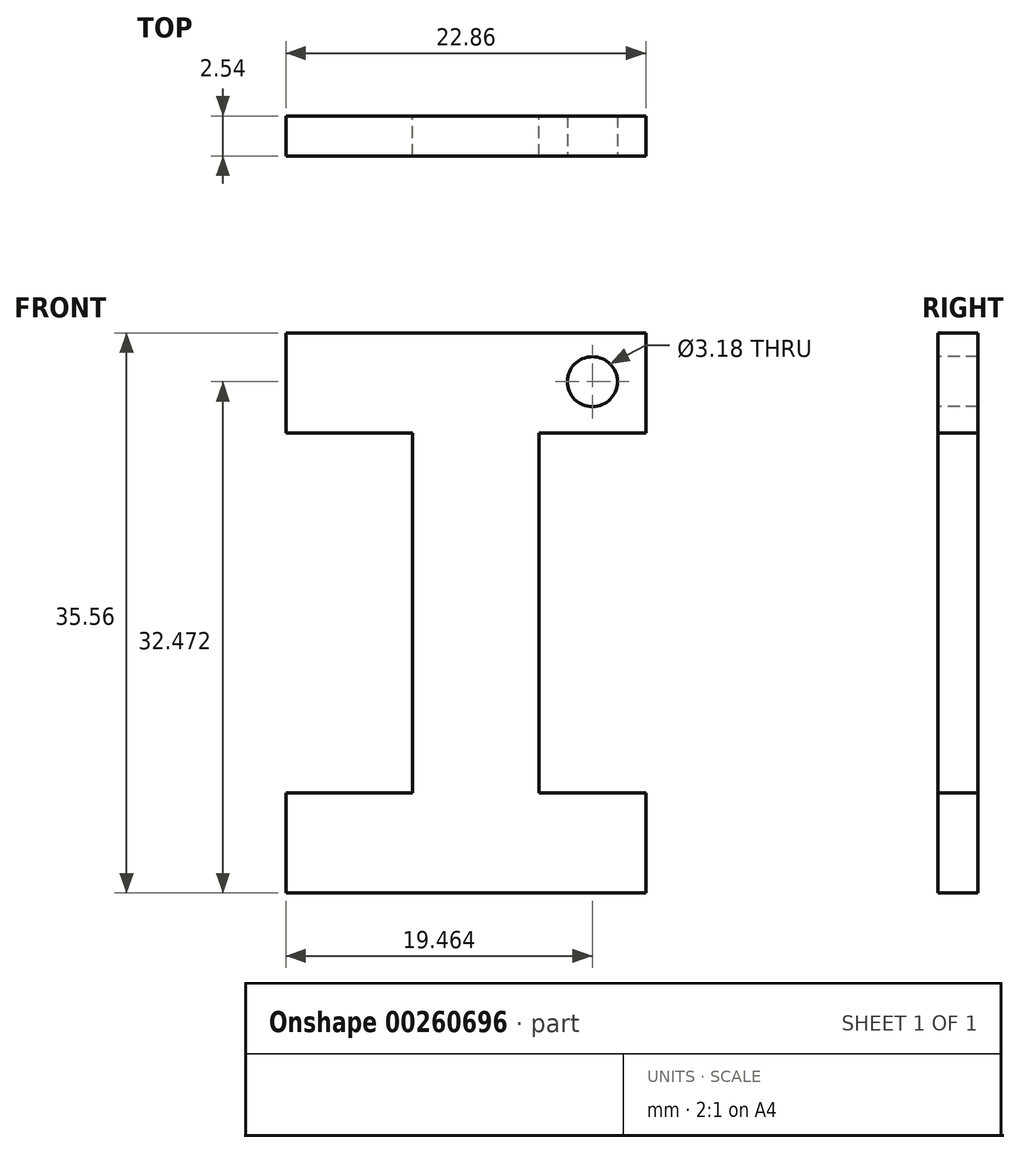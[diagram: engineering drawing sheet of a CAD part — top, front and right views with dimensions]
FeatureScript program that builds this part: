
annotation { "Feature Type Name" : "Feature", "Feature Type Description" : "" }
export const myFeature = defineFeature(function(context is Context, id is Id, definition is map)
    precondition{}
    {
        {
            var Q0;
            Q0=qCreatedBy(makeId("Front.planeOp"),FACE);
            var sketch = newSketch(context, id + "F0", { "sketchPlane" : qUnion([Q0])});
            skLineSegment(sketch, "E0", {"start": v(-12.96, 0) * mm, "end": v(-12.96, 6.35) * mm});
            skLineSegment(sketch, "E1", {"start": v(-12.96, 6.35) * mm, "end": v(-4.93, 6.35) * mm});
            skLineSegment(sketch, "E2", {"start": v(-4.93, 6.35) * mm, "end": v(-4.93, 29.21) * mm});
            skLineSegment(sketch, "E3", {"start": v(-4.93, 29.21) * mm, "end": v(-12.96, 29.21) * mm});
            skLineSegment(sketch, "E4", {"start": v(-12.96, 29.21) * mm, "end": v(-12.96, 35.56) * mm});
            skLineSegment(sketch, "E5", {"start": v(-12.96, 35.56) * mm, "end": v(9.9, 35.56) * mm});
            skLineSegment(sketch, "E6", {"start": v(9.9, 35.56) * mm, "end": v(9.9, 29.21) * mm});
            skLineSegment(sketch, "E7", {"start": v(9.9, 29.21) * mm, "end": v(3.11, 29.21) * mm});
            skLineSegment(sketch, "E8", {"start": v(3.11, 29.21) * mm, "end": v(3.11, 6.35) * mm});
            skLineSegment(sketch, "E9", {"start": v(3.11, 6.35) * mm, "end": v(9.9, 6.35) * mm});
            skLineSegment(sketch, "E10", {"start": v(9.9, 6.35) * mm, "end": v(9.9, 0) * mm});
            skLineSegment(sketch, "E11", {"start": v(9.9, 0) * mm, "end": v(-12.96, 0) * mm});
            skSolve(sketch);
        }
        {
            var Q0;
            Q0=makeQuery(id+"F0.imprint","IMPRINT",FACE,{"disambiguationData":[TD([[makeQuery(id+"F0.imprint","IMPRINT",EDGE,{"derivedFrom":sQuery(id+"F0.wireOp",EDGE,"E0")}),-1.0]])]});
            extrude(context, id + "F1", {"entities" : qUnion([Q0]), "depth" : 2.54 * mm});
        }
        {
            var Q0;
            Q0=makeQuery(id+"F1.opExtrude","CAP_FACE",FACE,{"disambiguationData":[OSD([sQuery(id+"F0.wireOp",EDGE,"E0"),sQuery(id+"F0.wireOp",EDGE,"E1"),sQuery(id+"F0.wireOp",EDGE,"E2"),sQuery(id+"F0.wireOp",EDGE,"E3"),sQuery(id+"F0.wireOp",EDGE,"E4"),sQuery(id+"F0.wireOp",EDGE,"E5"),sQuery(id+"F0.wireOp",EDGE,"E6"),sQuery(id+"F0.wireOp",EDGE,"E7"),sQuery(id+"F0.wireOp",EDGE,"E8"),sQuery(id+"F0.wireOp",EDGE,"E9"),sQuery(id+"F0.wireOp",EDGE,"E10"),sQuery(id+"F0.wireOp",EDGE,"E11")])],"isStart":false});
            var sketch = newSketch(context, id + "F2", { "sketchPlane" : qUnion([Q0])});
            skCircle(sketch, "E12", {"center": v(6.5, 32.47) * mm, "radius": 1.59 * mm});
            skPoint(sketch, "E12.centerSnap0", {"position": v(6.5, 29.21) * mm});
            skSolve(sketch);
        }
        {
            var Q0;
            Q0=makeQuery(id+"F2.imprint","IMPRINT",FACE,{"disambiguationData":[TD([[makeQuery(id+"F2.imprint","IMPRINT",EDGE,{"derivedFrom":sQuery(id+"F2.wireOp",EDGE,"E12")}),1.0]])]});
            extrude(context, id + "F3", {"entities" : qUnion([Q0]), "operationType" : NewBodyOperationType.REMOVE, "oppositeDirection" : true, "depth" : 2.54 * mm});
        }
    });
